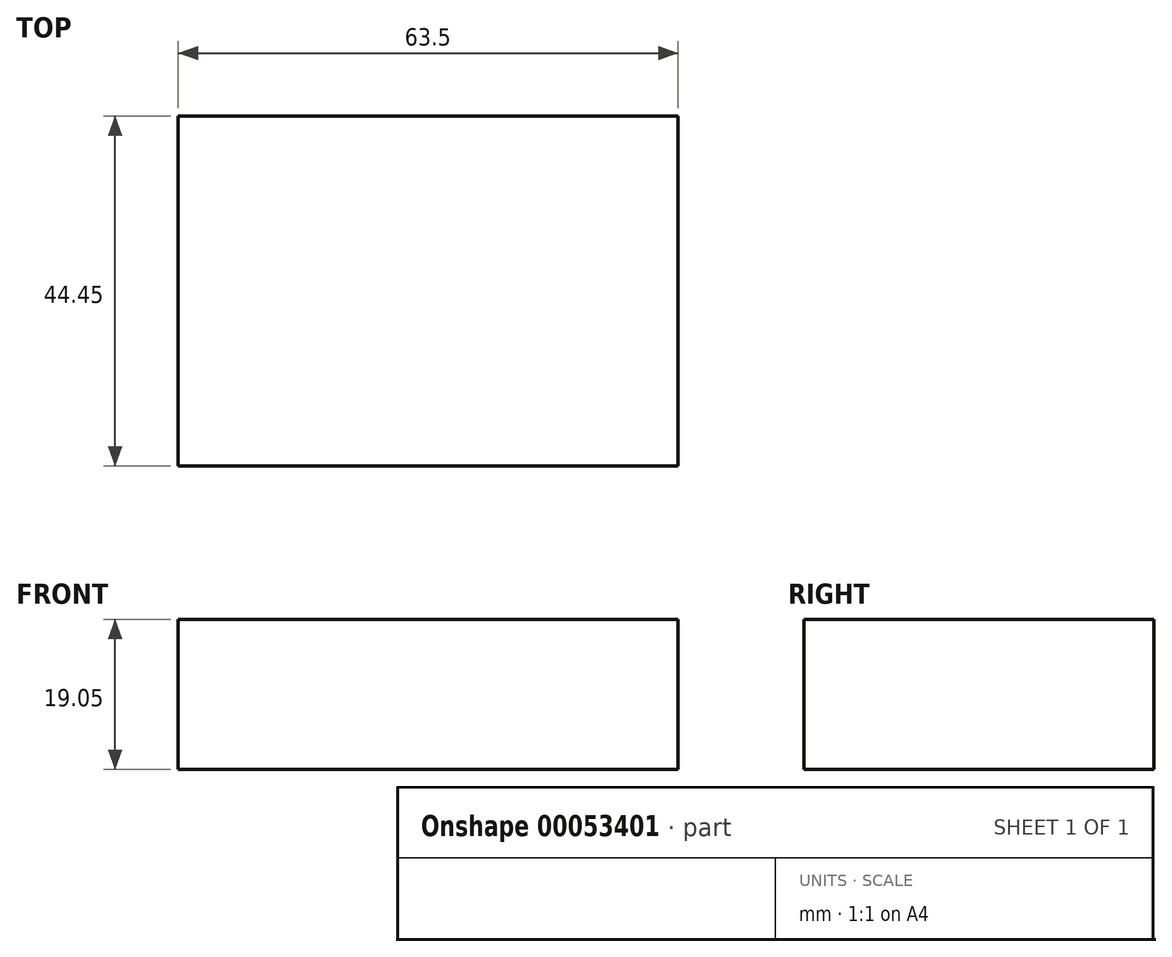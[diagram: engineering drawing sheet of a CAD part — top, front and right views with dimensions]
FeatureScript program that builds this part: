
annotation { "Feature Type Name" : "Feature", "Feature Type Description" : "" }
export const myFeature = defineFeature(function(context is Context, id is Id, definition is map)
    precondition{}
    {
        {
            var Q0;
            Q0=qCreatedBy(makeId("Top.planeOp"),FACE);
            var sketch = newSketch(context, id + "F0", { "sketchPlane" : qUnion([Q0])});
            skLineSegment(sketch, "E0.bottom", {"start": v(-35.36, 20.87) * mm, "end": v(28.14, 20.87) * mm});
            skLineSegment(sketch, "E0.top", {"start": v(-35.36, -23.58) * mm, "end": v(28.14, -23.58) * mm});
            skLineSegment(sketch, "E0.left", {"start": v(-35.36, 20.87) * mm, "end": v(-35.36, -23.58) * mm});
            skLineSegment(sketch, "E0.right", {"start": v(28.14, 20.87) * mm, "end": v(28.14, -23.58) * mm});
            skSolve(sketch);
        }
        {
            var Q0;
            Q0 = qSketchRegion(id + "F0", true);
            extrude(context, id + "F1", {"entities" : qUnion([Q0]), "depth" : 19.05 * mm});
        }
    });
